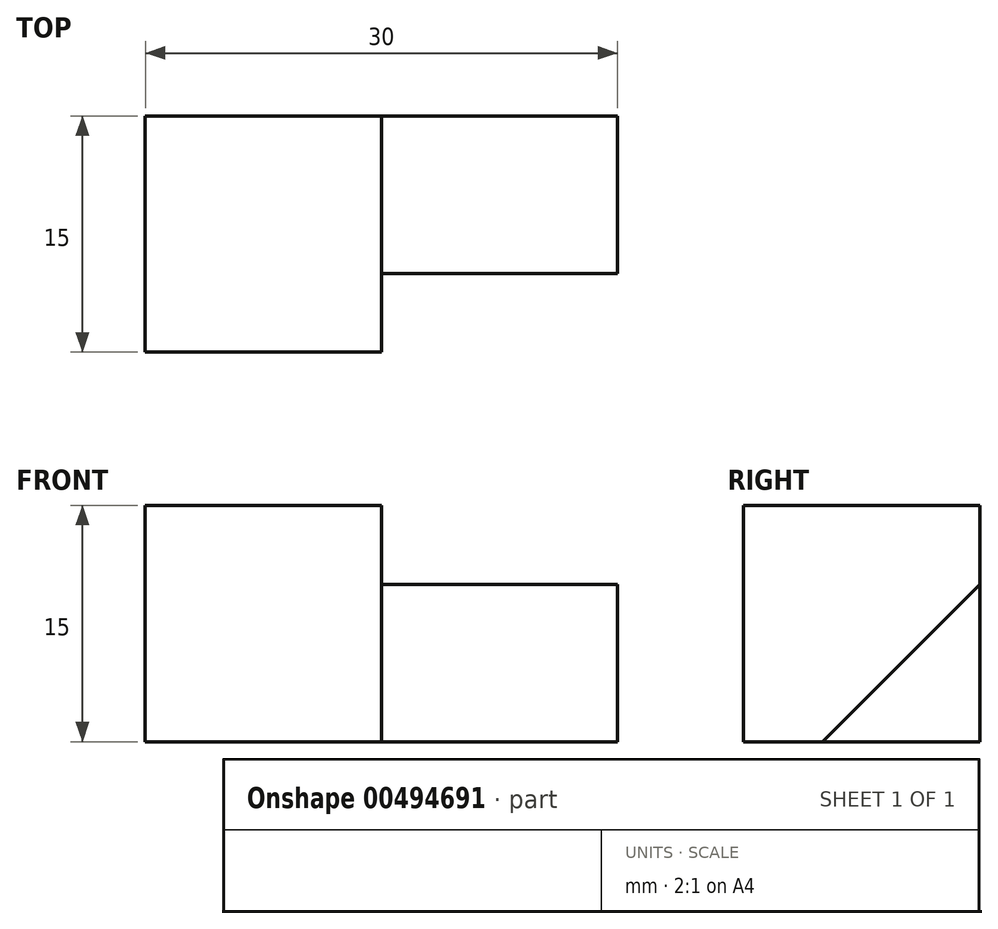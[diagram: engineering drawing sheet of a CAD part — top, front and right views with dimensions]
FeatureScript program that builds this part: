
annotation { "Feature Type Name" : "Feature", "Feature Type Description" : "" }
export const myFeature = defineFeature(function(context is Context, id is Id, definition is map)
    precondition{}
    {
        {
            var Q0;
            Q0=qCreatedBy(makeId("Top.planeOp"),FACE);
            var sketch = newSketch(context, id + "F0", { "sketchPlane" : qUnion([Q0])});
            skLineSegment(sketch, "E0.bottom", {"start": v(-58.88, -53.76) * mm, "end": v(-43.88, -53.76) * mm});
            skLineSegment(sketch, "E0.top", {"start": v(-58.88, -38.76) * mm, "end": v(-43.88, -38.76) * mm});
            skLineSegment(sketch, "E0.left", {"start": v(-58.88, -53.76) * mm, "end": v(-58.88, -38.76) * mm});
            skLineSegment(sketch, "E0.right", {"start": v(-43.88, -53.76) * mm, "end": v(-43.88, -38.76) * mm});
            skSolve(sketch);
        }
        {
            var Q0;
            Q0=qSketchRegion(id+"F0",true);
            extrude(context, id + "F1", {"entities" : qUnion([Q0]), "depth" : 15 * mm});
        }
        {
            var Q0;
            Q0=makeQuery(id+"F1.opExtrude","SWEPT_FACE",FACE,{"disambiguationData":[OSD([sQuery(id+"F0.wireOp",EDGE,"E0.right")])]});
            var sketch = newSketch(context, id + "F2", { "sketchPlane" : qUnion([Q0])});
            skLineSegment(sketch, "E1.bottom", {"start": v(-38.76, 0) * mm, "end": v(-48.76, 0) * mm});
            skLineSegment(sketch, "E1.top", {"start": v(-38.76, 10) * mm, "end": v(-48.76, 10) * mm});
            skLineSegment(sketch, "E1.left", {"start": v(-38.76, 0) * mm, "end": v(-38.76, 10) * mm});
            skLineSegment(sketch, "E1.right", {"start": v(-48.76, 0) * mm, "end": v(-48.76, 10) * mm});
            skSolve(sketch);
        }
        {
            var Q0;
            Q0=qSketchRegion(id+"F2",true);
            extrude(context, id + "F3", {"entities" : qUnion([Q0]), "operationType" : NewBodyOperationType.ADD, "depth" : 15 * mm});
        }
        {
            var Q0;
            Q0=makeQuery(id+"F3.opExtrude","CAP_FACE",FACE,{"disambiguationData":[OSD([sQuery(id+"F2.wireOp",EDGE,"E1.bottom"),sQuery(id+"F2.wireOp",EDGE,"E1.top"),sQuery(id+"F2.wireOp",EDGE,"E1.left"),sQuery(id+"F2.wireOp",EDGE,"E1.right")])],"isStart":false});
            var sketch = newSketch(context, id + "F4", { "sketchPlane" : qUnion([Q0])});
            skLineSegment(sketch, "E2", {"start": v(-38.76, 10) * mm, "end": v(-48.76, 0) * mm});
            skLineSegment(sketch, "E3", {"start": v(-48.76, 0) * mm, "end": v(-48.76, 10) * mm});
            skLineSegment(sketch, "E4", {"start": v(-48.76, 10) * mm, "end": v(-38.76, 10) * mm});
            skSolve(sketch);
        }
        {
            var Q0;
            Q0=qSketchRegion(id+"F4",true);
            extrude(context, id + "F5", {"entities" : qUnion([Q0]), "operationType" : NewBodyOperationType.REMOVE, "oppositeDirection" : true, "depth" : 15 * mm});
        }
    });
